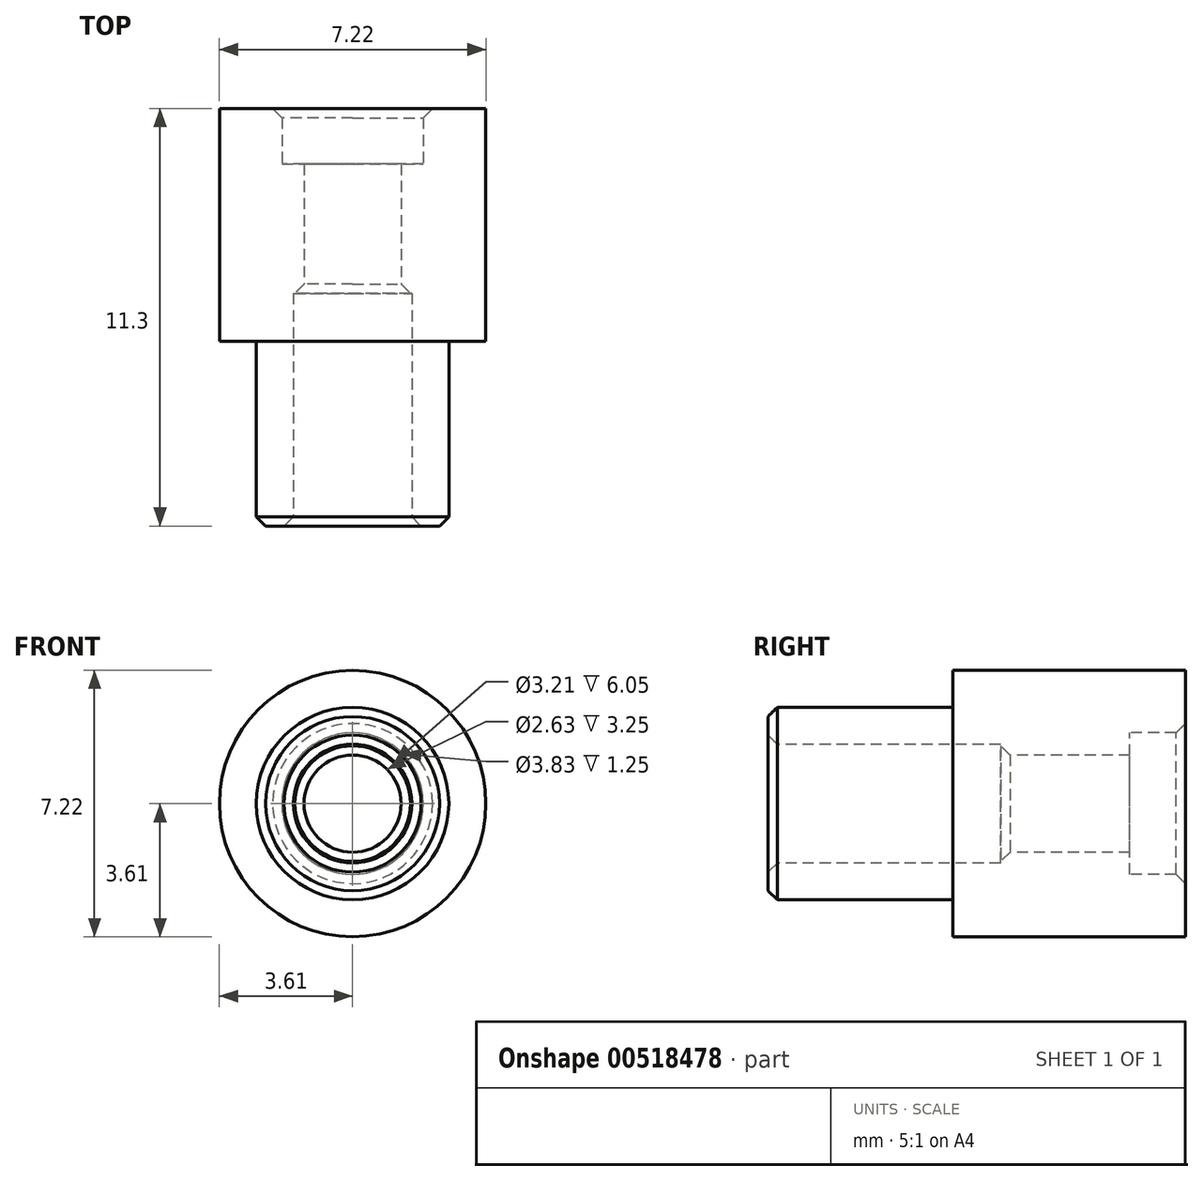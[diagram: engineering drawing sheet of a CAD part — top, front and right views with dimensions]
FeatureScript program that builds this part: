
annotation { "Feature Type Name" : "Feature", "Feature Type Description" : "" }
export const myFeature = defineFeature(function(context is Context, id is Id, definition is map)
    precondition{}
    {
        {
            var Q0;
            Q0=qCreatedBy(makeId("Right.planeOp"),FACE);
            var sketch = newSketch(context, id + "F0", { "sketchPlane" : qUnion([Q0])});
            skLineSegment(sketch, "E0", {"start": v(-7.9, 2.6) * mm, "end": v(-7.9, 1.6) * mm});
            skLineSegment(sketch, "E1", {"start": v(-7.9, 1.6) * mm, "end": v(-1.6, 1.6) * mm});
            skLineSegment(sketch, "E2", {"start": v(-1.6, 1.6) * mm, "end": v(-1.6, 1.31) * mm});
            skLineSegment(sketch, "E3", {"start": v(-1.6, 1.31) * mm, "end": v(1.9, 1.31) * mm});
            skLineSegment(sketch, "E4", {"start": v(1.9, 1.31) * mm, "end": v(1.9, 1.92) * mm});
            skLineSegment(sketch, "E5", {"start": v(1.9, 1.92) * mm, "end": v(3.4, 1.92) * mm});
            skLineSegment(sketch, "E6", {"start": v(-7.9, 2.6) * mm, "end": v(-2.9, 2.6) * mm});
            skLineSegment(sketch, "E7", {"start": v(-2.9, 2.6) * mm, "end": v(-2.9, 3.6) * mm});
            skLineSegment(sketch, "E8", {"start": v(-2.9, 3.6) * mm, "end": v(3.4, 3.6) * mm});
            skLineSegment(sketch, "E9", {"start": v(3.4, 3.6) * mm, "end": v(3.4, 1.91) * mm});
            skLineSegment(sketch, "E10", {"start": v(-10.16, 0) * mm, "end": v(6.88, 0) * mm, "construction": true});
            skLineSegment(sketch, "E11.MirrorCS", {"start": v(-1.6, -1.31) * mm, "end": v(1.9, -1.31) * mm, "construction": true});
            skLineSegment(sketch, "E12.MirrorCS", {"start": v(-7.9, -1.6) * mm, "end": v(-1.6, -1.6) * mm, "construction": true});
            skLineSegment(sketch, "E13.MirrorCS", {"start": v(1.9, -1.92) * mm, "end": v(3.4, -1.92) * mm, "construction": true});
            skLineSegment(sketch, "E14.MirrorCS", {"start": v(-7.9, -2.6) * mm, "end": v(-2.9, -2.6) * mm, "construction": true});
            skLineSegment(sketch, "E15.MirrorCS", {"start": v(-2.9, -3.6) * mm, "end": v(3.4, -3.6) * mm, "construction": true});
            skSolve(sketch);
        }
        {
            var Q0;
            Q0=qSketchRegion(id+"F0",true);
            var Q1;
            Q1=sQuery(id+"F0.wireOp",EDGE,"E10");
            revolve(context, id + "F1", {"entities" : qUnion([Q0]), "axis" : qUnion([Q1]), "revolveType" : RevolveType.FULL});
        }
        {
            var Q0;
            Q0=makeQuery(id+"F1.opRevolve","SWEPT_EDGE",EDGE,{"disambiguationData":[OSD([sQuery(id+"F0.wireOp",EDGE,"E5"),sQuery(id+"F0.wireOp",EDGE,"E9")])]});
            var Q1;
            Q1=makeQuery(id+"F1.opRevolve","SWEPT_EDGE",EDGE,{"disambiguationData":[OSD([sQuery(id+"F0.wireOp",EDGE,"E0"),sQuery(id+"F0.wireOp",EDGE,"E1")])]});
            var Q2;
            Q2=makeQuery(id+"F1.opRevolve","SWEPT_EDGE",EDGE,{"disambiguationData":[OSD([sQuery(id+"F0.wireOp",EDGE,"E0"),sQuery(id+"F0.wireOp",EDGE,"E6")])]});
            var Q3;
            Q3=makeQuery(id+"F1.opRevolve","SWEPT_EDGE",EDGE,{"disambiguationData":[OSD([sQuery(id+"F0.wireOp",EDGE,"E2"),sQuery(id+"F0.wireOp",EDGE,"E3")])]});
            chamfer(context, id + "F2", {"entities" : qUnion([Q0, Q1, Q2, Q3]), "width" : .25 * mm, "tangentPropagation" : true});
        }
    });
